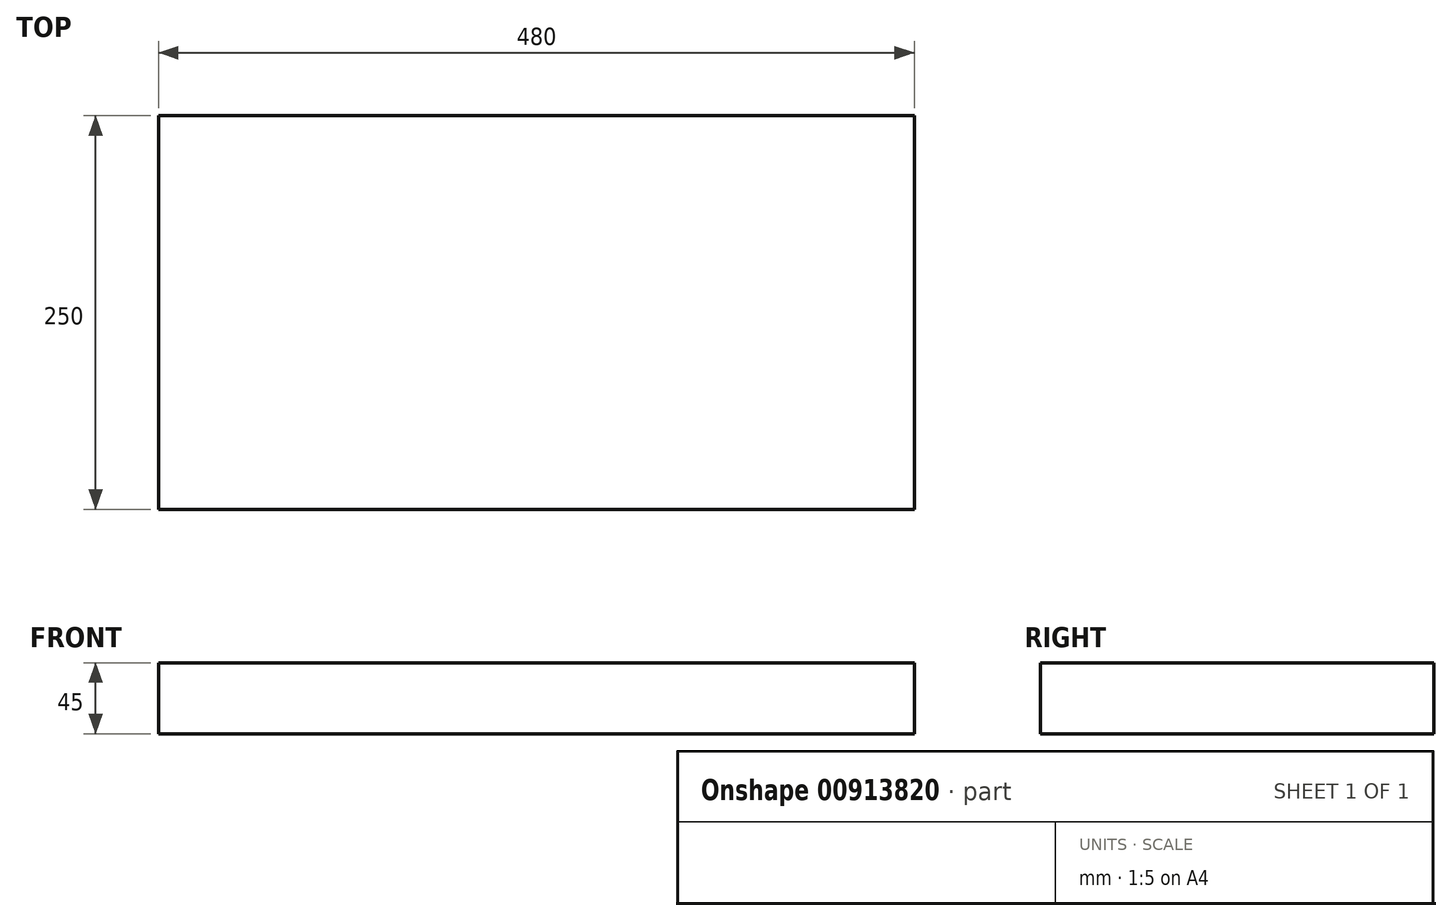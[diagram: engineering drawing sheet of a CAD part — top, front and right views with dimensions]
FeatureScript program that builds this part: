
annotation { "Feature Type Name" : "Feature", "Feature Type Description" : "" }
export const myFeature = defineFeature(function(context is Context, id is Id, definition is map)
    precondition{}
    {
        {
            var Q0;
            Q0=qCreatedBy(makeId("Top.planeOp"),FACE);
            var sketch = newSketch(context, id + "F0", { "sketchPlane" : qUnion([Q0])});
            skLineSegment(sketch, "E0.bottom", {"start": v(240, -125) * mm, "end": v(-240, -125) * mm});
            skLineSegment(sketch, "E0.top", {"start": v(240, 125) * mm, "end": v(-240, 125) * mm});
            skLineSegment(sketch, "E0.left", {"start": v(240, -125) * mm, "end": v(240, 125) * mm});
            skLineSegment(sketch, "E0.right", {"start": v(-240, -125) * mm, "end": v(-240, 125) * mm});
            skPoint(sketch, "E0.middle", {"position": v(0, 0) * mm});
            skSolve(sketch);
        }
        {
            var Q0;
            Q0=makeQuery(id+"F0.imprint","IMPRINT",FACE,{"disambiguationData":[TD([[makeQuery(id+"F0.imprint","IMPRINT",EDGE,{"derivedFrom":sQuery(id+"F0.wireOp",EDGE,"E0.bottom")}),-1.0]])]});
            extrude(context, id + "F1", {"entities" : qUnion([Q0]), "depth" : 45 * mm, "offsetDistance" : 25 * mm});
        }
    });
